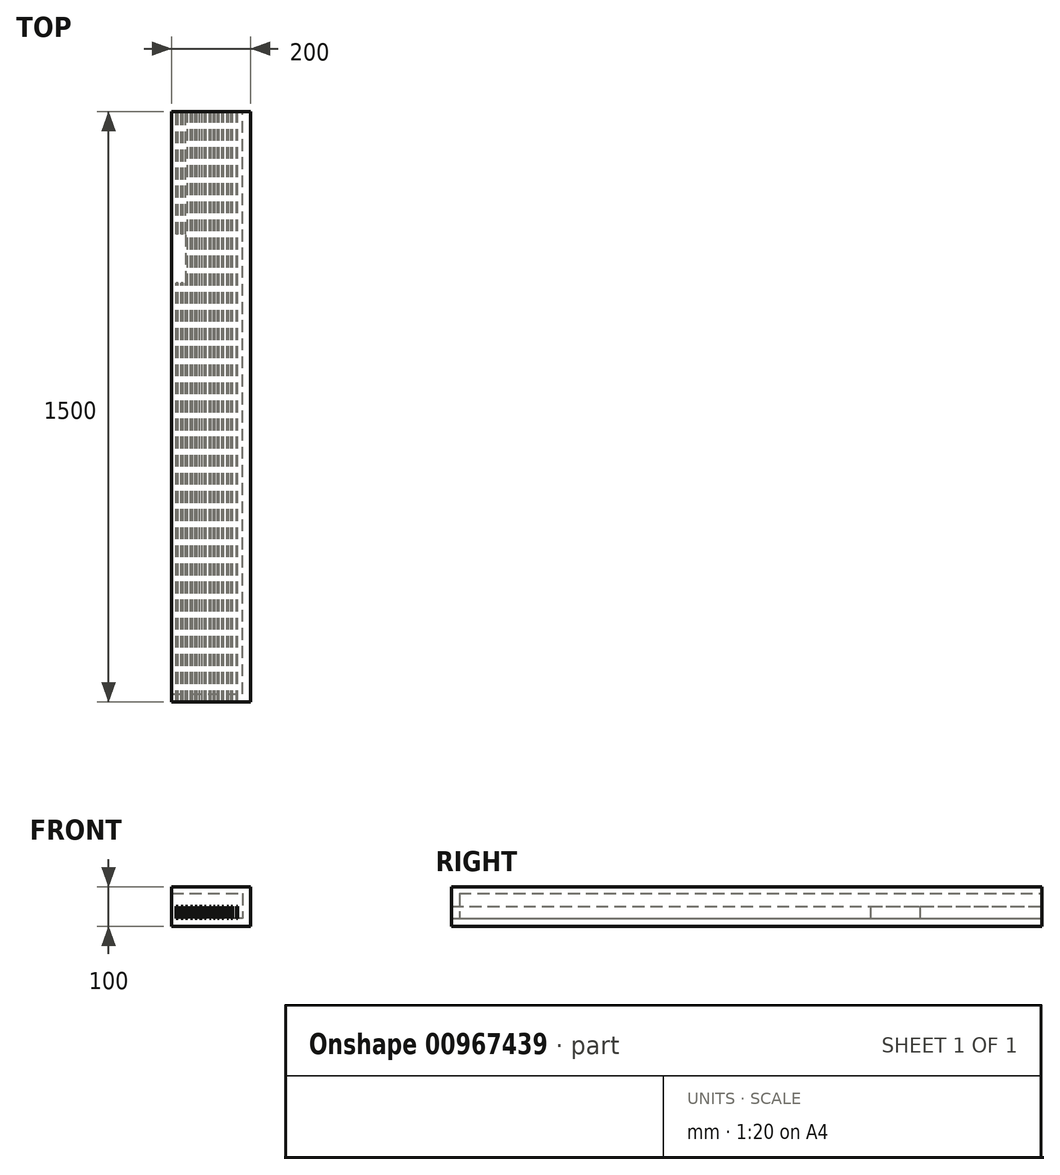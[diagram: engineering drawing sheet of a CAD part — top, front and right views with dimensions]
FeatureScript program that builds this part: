
annotation { "Feature Type Name" : "Feature", "Feature Type Description" : "" }
export const myFeature = defineFeature(function(context is Context, id is Id, definition is map)
    precondition{}
    {
        {
            var Q0;
            Q0=qCreatedBy(makeId("Front.planeOp"),FACE);
            var sketch = newSketch(context, id + "F0", { "sketchPlane" : qUnion([Q0])});
            skLineSegment(sketch, "E0.bottom", {"start": v(-21.78, 92.39) * mm, "end": v(178.22, 92.39) * mm});
            skLineSegment(sketch, "E0.top", {"start": v(-21.78, -7.61) * mm, "end": v(178.22, -7.61) * mm});
            skLineSegment(sketch, "E0.left", {"start": v(-21.78, 92.39) * mm, "end": v(-21.78, -7.61) * mm});
            skLineSegment(sketch, "E0.right", {"start": v(178.22, 92.39) * mm, "end": v(178.22, -7.61) * mm});
            skSolve(sketch);
        }
        {
            var Q0;
            Q0 = qSketchRegion(id + "F0", true);
            extrude(context, id + "F1", {"entities" : qUnion([Q0]), "depth" : 1500 * mm, "offsetDistance" : 25 * mm});
        }
        {
            var Q0;
            Q0=makeQuery(id+"F1.opExtrude","CAP_FACE",FACE,{"disambiguationData":[OSD([sQuery(id+"F0.wireOp",EDGE,"E0.bottom"),sQuery(id+"F0.wireOp",EDGE,"E0.top"),sQuery(id+"F0.wireOp",EDGE,"E0.left"),sQuery(id+"F0.wireOp",EDGE,"E0.right")])],"isStart":true});
            var sketch = newSketch(context, id + "F2", { "sketchPlane" : qUnion([Q0])});
            skLineSegment(sketch, "E1", {"start": v(21.78, 76.25) * mm, "end": v(-158.29, 76.25) * mm});
            skLineSegment(sketch, "E2", {"start": v(-158.29, 76.25) * mm, "end": v(-158.29, 12.07) * mm});
            skLineSegment(sketch, "E3", {"start": v(-158.29, 12.07) * mm, "end": v(21.78, 12.07) * mm});
            skLineSegment(sketch, "E4", {"start": v(21.78, 12.07) * mm, "end": v(21.78, 76.25) * mm});
            skSolve(sketch);
        }
        {
            var Q0;
            Q0 = qSketchRegion(id + "F2", true);
            extrude(context, id + "F3", {"entities" : qUnion([Q0]), "operationType" : NewBodyOperationType.REMOVE, "oppositeDirection" : true, "depth" : 1480 * mm, "offsetDistance" : 25 * mm});
        }
        {
            var Q0;
            Q0=makeQuery(id+"F1.opExtrude","CAP_FACE",FACE,{"disambiguationData":[OSD([sQuery(id+"F0.wireOp",EDGE,"E0.bottom"),sQuery(id+"F0.wireOp",EDGE,"E0.top"),sQuery(id+"F0.wireOp",EDGE,"E0.left"),sQuery(id+"F0.wireOp",EDGE,"E0.right")])],"isStart":true});
            var sketch = newSketch(context, id + "F4", { "sketchPlane" : qUnion([Q0])});
            skLineSegment(sketch, "E5", {"start": v(-146.04, 12.07) * mm, "end": v(-146.04, 43.1) * mm});
            skLineSegment(sketch, "E6", {"start": v(-146.04, 43.1) * mm, "end": v(-142.54, 43.1) * mm});
            skLineSegment(sketch, "E7", {"start": v(-142.54, 43.1) * mm, "end": v(-142.54, 12.07) * mm});
            skLineSegment(sketch, "E8", {"start": v(-142.54, 12.07) * mm, "end": v(-146.04, 12.07) * mm});
            skLineSegment(sketch, "E9", {"start": v(-132.93, 12.07) * mm, "end": v(-132.93, 43.1) * mm});
            skLineSegment(sketch, "E10", {"start": v(-132.93, 43.1) * mm, "end": v(-129.43, 43.1) * mm});
            skLineSegment(sketch, "E11", {"start": v(-129.43, 43.1) * mm, "end": v(-129.43, 12.07) * mm});
            skLineSegment(sketch, "E12", {"start": v(-129.43, 12.07) * mm, "end": v(-132.93, 12.07) * mm});
            skLineSegment(sketch, "E13", {"start": v(-122.21, 12.07) * mm, "end": v(-122.21, 43.1) * mm});
            skLineSegment(sketch, "E14", {"start": v(-122.21, 43.1) * mm, "end": v(-118.71, 43.1) * mm});
            skLineSegment(sketch, "E15", {"start": v(-118.71, 43.1) * mm, "end": v(-118.71, 12.07) * mm});
            skLineSegment(sketch, "E16", {"start": v(-118.71, 12.07) * mm, "end": v(-122.21, 12.07) * mm});
            skLineSegment(sketch, "E17", {"start": v(-110, 12.07) * mm, "end": v(-110, 43.1) * mm});
            skLineSegment(sketch, "E18", {"start": v(-110, 43.1) * mm, "end": v(-106.5, 43.1) * mm});
            skLineSegment(sketch, "E19", {"start": v(-106.5, 43.1) * mm, "end": v(-106.5, 12.07) * mm});
            skLineSegment(sketch, "E20", {"start": v(-106.5, 12.07) * mm, "end": v(-110, 12.07) * mm});
            skLineSegment(sketch, "E21", {"start": v(-98.66, 12.07) * mm, "end": v(-98.66, 43.1) * mm});
            skLineSegment(sketch, "E22", {"start": v(-98.66, 43.1) * mm, "end": v(-95.16, 43.1) * mm});
            skLineSegment(sketch, "E23", {"start": v(-95.16, 43.1) * mm, "end": v(-95.16, 12.07) * mm});
            skLineSegment(sketch, "E24", {"start": v(-95.16, 12.07) * mm, "end": v(-98.66, 12.07) * mm});
            skLineSegment(sketch, "E25", {"start": v(-88.27, 12.07) * mm, "end": v(-88.27, 43.1) * mm});
            skLineSegment(sketch, "E26", {"start": v(-88.27, 43.1) * mm, "end": v(-84.77, 43.1) * mm});
            skLineSegment(sketch, "E27", {"start": v(-84.77, 43.1) * mm, "end": v(-84.77, 12.07) * mm});
            skLineSegment(sketch, "E28", {"start": v(-84.77, 12.07) * mm, "end": v(-88.27, 12.07) * mm});
            skLineSegment(sketch, "E29", {"start": v(-77.78, 12.07) * mm, "end": v(-77.78, 43.1) * mm});
            skLineSegment(sketch, "E30", {"start": v(-77.78, 43.1) * mm, "end": v(-74.28, 43.1) * mm});
            skLineSegment(sketch, "E31", {"start": v(-74.28, 43.1) * mm, "end": v(-74.28, 12.07) * mm});
            skLineSegment(sketch, "E32", {"start": v(-74.28, 12.07) * mm, "end": v(-77.78, 12.07) * mm});
            skLineSegment(sketch, "E33", {"start": v(-65.75, 12.07) * mm, "end": v(-65.75, 43.1) * mm});
            skLineSegment(sketch, "E34", {"start": v(-65.75, 43.1) * mm, "end": v(-61.67, 43.1) * mm});
            skLineSegment(sketch, "E35", {"start": v(-61.67, 43.1) * mm, "end": v(-61.67, 12.07) * mm});
            skLineSegment(sketch, "E36", {"start": v(-61.67, 12.07) * mm, "end": v(-65.75, 12.07) * mm});
            skLineSegment(sketch, "E37", {"start": v(-55.43, 12.07) * mm, "end": v(-55.43, 43.1) * mm});
            skLineSegment(sketch, "E38", {"start": v(-55.43, 43.1) * mm, "end": v(-49.68, 43.1) * mm});
            skLineSegment(sketch, "E39", {"start": v(-49.68, 43.1) * mm, "end": v(-49.68, 12.07) * mm});
            skLineSegment(sketch, "E40", {"start": v(-49.68, 12.07) * mm, "end": v(-55.43, 12.07) * mm});
            skLineSegment(sketch, "E41", {"start": v(-42.96, 12.07) * mm, "end": v(-42.96, 43.1) * mm});
            skLineSegment(sketch, "E42", {"start": v(-42.96, 43.1) * mm, "end": v(-38.16, 43.1) * mm});
            skLineSegment(sketch, "E43", {"start": v(-38.16, 43.1) * mm, "end": v(-38.16, 12.07) * mm});
            skLineSegment(sketch, "E44", {"start": v(-38.16, 12.07) * mm, "end": v(-42.96, 12.07) * mm});
            skLineSegment(sketch, "E45", {"start": v(-31.45, 12.07) * mm, "end": v(-31.45, 43.1) * mm});
            skLineSegment(sketch, "E46", {"start": v(-31.45, 43.1) * mm, "end": v(-26.65, 43.1) * mm});
            skLineSegment(sketch, "E47", {"start": v(-26.65, 43.1) * mm, "end": v(-26.65, 12.07) * mm});
            skLineSegment(sketch, "E48", {"start": v(-26.65, 12.07) * mm, "end": v(-31.45, 12.07) * mm});
            skLineSegment(sketch, "E49", {"start": v(-18.97, 12.07) * mm, "end": v(-18.97, 43.1) * mm});
            skLineSegment(sketch, "E50", {"start": v(-18.97, 43.1) * mm, "end": v(-13.7, 43.1) * mm});
            skLineSegment(sketch, "E51", {"start": v(-13.7, 43.1) * mm, "end": v(-13.7, 12.07) * mm});
            skLineSegment(sketch, "E52", {"start": v(-13.7, 12.07) * mm, "end": v(-18.97, 12.07) * mm});
            skLineSegment(sketch, "E53", {"start": v(-7.46, 12.07) * mm, "end": v(-7.46, 43.1) * mm});
            skLineSegment(sketch, "E54", {"start": v(-7.46, 43.1) * mm, "end": v(-2.42, 43.1) * mm});
            skLineSegment(sketch, "E55", {"start": v(-2.42, 43.1) * mm, "end": v(-2.42, 12.07) * mm});
            skLineSegment(sketch, "E56", {"start": v(-2.42, 12.07) * mm, "end": v(-7.46, 12.07) * mm});
            skLineSegment(sketch, "E57", {"start": v(5.5, 12.07) * mm, "end": v(5.5, 43.1) * mm});
            skLineSegment(sketch, "E58", {"start": v(5.5, 43.1) * mm, "end": v(10.05, 43.1) * mm});
            skLineSegment(sketch, "E59", {"start": v(10.05, 43.1) * mm, "end": v(10.05, 12.07) * mm});
            skLineSegment(sketch, "E60", {"start": v(10.05, 12.07) * mm, "end": v(5.5, 12.07) * mm});
            skSolve(sketch);
        }
        {
            var Q0;
            Q0 = qSketchRegion(id + "F4", true);
            extrude(context, id + "F5", {"entities" : qUnion([Q0]), "oppositeDirection" : true, "depth" : 1500 * mm, "offsetDistance" : 25 * mm});
        }
        {
            var Q0;
            Q0=makeQuery(id+"F5.opExtrude","SWEPT_FACE",FACE,{"disambiguationData":[OSD([sQuery(id+"F4.wireOp",EDGE,"E59")])]});
            var sketch = newSketch(context, id + "F6", { "sketchPlane" : qUnion([Q0])});
            skLineSegment(sketch, "E61.bottom", {"start": v(310.55, 43.1) * mm, "end": v(435.04, 43.1) * mm});
            skLineSegment(sketch, "E61.top", {"start": v(310.55, 12.07) * mm, "end": v(435.04, 12.07) * mm});
            skLineSegment(sketch, "E61.left", {"start": v(310.55, 43.1) * mm, "end": v(310.55, 12.07) * mm});
            skLineSegment(sketch, "E61.right", {"start": v(435.04, 43.1) * mm, "end": v(435.04, 12.07) * mm});
            skSolve(sketch);
        }
        {
            var Q0;
            Q0=makeQuery(id+"F6.imprint","IMPRINT",FACE,{"disambiguationData":[TD([[makeQuery(id+"F6.imprint","IMPRINT",EDGE,{"derivedFrom":sQuery(id+"F6.wireOp",EDGE,"E61.bottom")}),1.0]])]});
            extrude(context, id + "F7", {"entities" : qUnion([Q0]), "operationType" : NewBodyOperationType.REMOVE, "oppositeDirection" : true, "depth" : 25 * mm, "offsetDistance" : 25 * mm});
        }
    });
